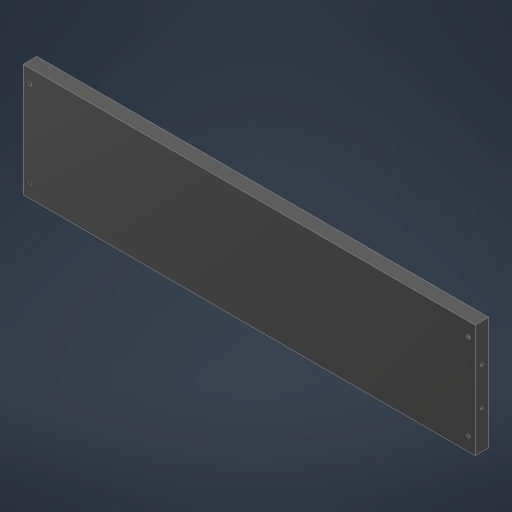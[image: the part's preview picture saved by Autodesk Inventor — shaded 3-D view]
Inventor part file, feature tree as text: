
AUTODESK INVENTOR PART (.ipt)
format: ipt  version: 2024 (Build 280153000, 153)  size: 210,432 bytes
history: native  units: in
note: dims shown in document units (in); Inventor stores cm internally (conversion verified against a paired STEP export)
features: other x1, extrude x1, sketch x1
ambient origin geometry x8: Origin, YZ Plane, XZ Plane, XY Plane, X Axis, Y Axis, Z Axis, Center Point
bodies: Body1 (feature_tree)
feature tree (3):
  other  "Sólido1"
  extrude  "Extrusión1"  Depth=0.7087in
  sketch  "Boceto1"  dims[d0=0.1575in d1=0.1575in d2=1.9685in d3=1.9685in d4=1.9685in d5=0.7087in d6=0.3543in d7=31.4961in d8=0.0in]
